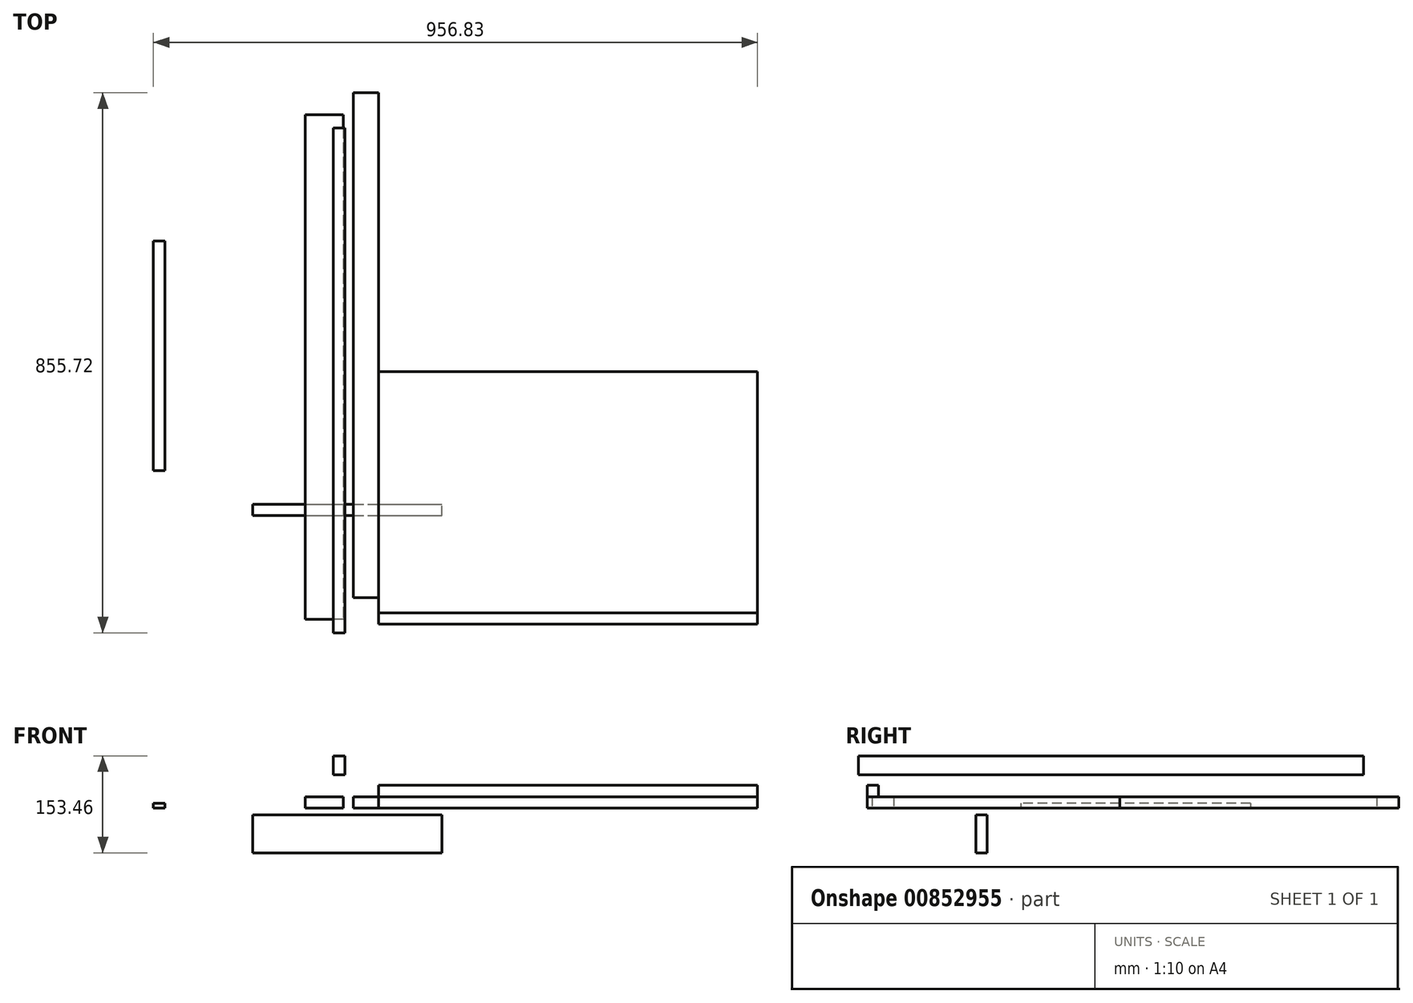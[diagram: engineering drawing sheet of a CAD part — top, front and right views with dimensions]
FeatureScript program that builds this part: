
annotation { "Feature Type Name" : "Feature", "Feature Type Description" : "" }
export const myFeature = defineFeature(function(context is Context, id is Id, definition is map)
    precondition{}
    {
        {
            var Q0;
            Q0=qCreatedBy(makeId("Top.planeOp"),FACE);
            var sketch = newSketch(context, id + "F0", { "sketchPlane" : qUnion([Q0])});
            skLineSegment(sketch, "E0.bottom", {"start": v(15.54, 617.3) * mm, "end": v(-44.46, 617.3) * mm});
            skLineSegment(sketch, "E0.top", {"start": v(15.54, -182.7) * mm, "end": v(-44.46, -182.7) * mm});
            skLineSegment(sketch, "E0.left", {"start": v(15.54, 617.3) * mm, "end": v(15.54, -182.7) * mm});
            skLineSegment(sketch, "E0.right", {"start": v(-44.46, 617.3) * mm, "end": v(-44.46, -182.7) * mm});
            skSolve(sketch);
        }
        {
            var Q0;
            Q0 = qSketchRegion(id + "F0", true);
            extrude(context, id + "F1", {"entities" : qUnion([Q0]), "depth" : 18 * mm, "offsetDistance" : 25 * mm});
        }
        {
            var Q0;
            Q0=qCreatedBy(makeId("Top.planeOp"),FACE);
            var sketch = newSketch(context, id + "F2", { "sketchPlane" : qUnion([Q0])});
            skLineSegment(sketch, "E1.bottom", {"start": v(31.45, 651.75) * mm, "end": v(71.45, 651.75) * mm});
            skLineSegment(sketch, "E1.top", {"start": v(31.45, -148.25) * mm, "end": v(71.45, -148.25) * mm});
            skLineSegment(sketch, "E1.left", {"start": v(31.45, 651.75) * mm, "end": v(31.45, -148.25) * mm});
            skLineSegment(sketch, "E1.right", {"start": v(71.45, 651.75) * mm, "end": v(71.45, -148.25) * mm});
            skSolve(sketch);
        }
        {
            var Q0;
            Q0 = qSketchRegion(id + "F2", true);
            extrude(context, id + "F3", {"entities" : qUnion([Q0]), "depth" : 18 * mm, "offsetDistance" : 25 * mm});
        }
        {
            var Q0;
            Q0=qCreatedBy(makeId("Right.planeOp"),FACE);
            var sketch = newSketch(context, id + "F4", { "sketchPlane" : qUnion([Q0])});
            skLineSegment(sketch, "E2.bottom", {"start": v(-203.97, 82.66) * mm, "end": v(596.03, 82.66) * mm});
            skLineSegment(sketch, "E2.top", {"start": v(-203.97, 52.66) * mm, "end": v(596.03, 52.66) * mm});
            skLineSegment(sketch, "E2.left", {"start": v(-203.97, 82.66) * mm, "end": v(-203.97, 52.66) * mm});
            skLineSegment(sketch, "E2.right", {"start": v(596.03, 82.66) * mm, "end": v(596.03, 52.66) * mm});
            skSolve(sketch);
        }
        {
            var Q0;
            Q0 = qSketchRegion(id + "F4", true);
            extrude(context, id + "F5", {"entities" : qUnion([Q0]), "depth" : 18 * mm, "offsetDistance" : 25 * mm});
        }
        {
            var Q0;
            Q0=qCreatedBy(makeId("Front.planeOp"),FACE);
            var sketch = newSketch(context, id + "F6", { "sketchPlane" : qUnion([Q0])});
            skLineSegment(sketch, "E3.bottom", {"start": v(-127.98, -70.8) * mm, "end": v(172.02, -70.8) * mm});
            skLineSegment(sketch, "E3.top", {"start": v(-127.98, -10.8) * mm, "end": v(172.02, -10.8) * mm});
            skLineSegment(sketch, "E3.left", {"start": v(-127.98, -70.8) * mm, "end": v(-127.98, -10.8) * mm});
            skLineSegment(sketch, "E3.right", {"start": v(172.02, -70.8) * mm, "end": v(172.02, -10.8) * mm});
            skSolve(sketch);
        }
        {
            var Q0;
            Q0 = qSketchRegion(id + "F6", true);
            extrude(context, id + "F7", {"entities" : qUnion([Q0]), "depth" : 18 * mm, "offsetDistance" : 25 * mm});
        }
        {
            var Q0;
            Q0=qCreatedBy(makeId("Top.planeOp"),FACE);
            var sketch = newSketch(context, id + "F8", { "sketchPlane" : qUnion([Q0])});
            skLineSegment(sketch, "E4.bottom", {"start": v(71.63, 209.89) * mm, "end": v(671.63, 209.89) * mm});
            skLineSegment(sketch, "E4.top", {"start": v(71.63, -190.11) * mm, "end": v(671.63, -190.11) * mm});
            skLineSegment(sketch, "E4.left", {"start": v(71.63, 209.89) * mm, "end": v(71.63, -190.11) * mm});
            skLineSegment(sketch, "E4.right", {"start": v(671.63, 209.89) * mm, "end": v(671.63, -190.11) * mm});
            skSolve(sketch);
        }
        {
            var Q0;
            Q0 = qSketchRegion(id + "F8", true);
            extrude(context, id + "F9", {"entities" : qUnion([Q0]), "depth" : 18 * mm, "offsetDistance" : 25 * mm});
        }
        {
            var Q0;
            Q0=makeQuery(id+"F9.opExtrude","CAP_FACE",FACE,{"disambiguationData":[OSD([sQuery(id+"F8.wireOp",EDGE,"E4.bottom"),sQuery(id+"F8.wireOp",EDGE,"E4.top"),sQuery(id+"F8.wireOp",EDGE,"E4.left"),sQuery(id+"F8.wireOp",EDGE,"E4.right")])],"isStart":false});
            var sketch = newSketch(context, id + "F10", { "sketchPlane" : qUnion([Q0])});
            skLineSegment(sketch, "E5.bottom", {"start": v(71.63, -190.11) * mm, "end": v(671.63, -190.11) * mm});
            skLineSegment(sketch, "E5.top", {"start": v(71.63, -172.11) * mm, "end": v(671.63, -172.11) * mm});
            skLineSegment(sketch, "E5.left", {"start": v(71.63, -190.11) * mm, "end": v(71.63, -172.11) * mm});
            skLineSegment(sketch, "E5.right", {"start": v(671.63, -190.11) * mm, "end": v(671.63, -172.11) * mm});
            skSolve(sketch);
        }
        {
            var Q0;
            Q0 = qSketchRegion(id + "F10", true);
            extrude(context, id + "F11", {"entities" : qUnion([Q0]), "depth" : 18 * mm, "offsetDistance" : 25 * mm});
        }
        {
            var Q0;
            Q0=qCreatedBy(makeId("Top.planeOp"),FACE);
            var sketch = newSketch(context, id + "F12", { "sketchPlane" : qUnion([Q0])});
            skLineSegment(sketch, "E6.bottom", {"start": v(-267.2, 416.99) * mm, "end": v(-285.2, 416.99) * mm});
            skLineSegment(sketch, "E6.top", {"start": v(-267.2, 52.99) * mm, "end": v(-285.2, 52.99) * mm});
            skLineSegment(sketch, "E6.left", {"start": v(-267.2, 416.99) * mm, "end": v(-267.2, 52.99) * mm});
            skLineSegment(sketch, "E6.right", {"start": v(-285.2, 416.99) * mm, "end": v(-285.2, 52.99) * mm});
            skSolve(sketch);
        }
        {
            var Q0;
            Q0 = qSketchRegion(id + "F12", true);
            extrude(context, id + "F13", {"entities" : qUnion([Q0]), "depth" : 8 * mm, "offsetDistance" : 25 * mm});
        }
    });
